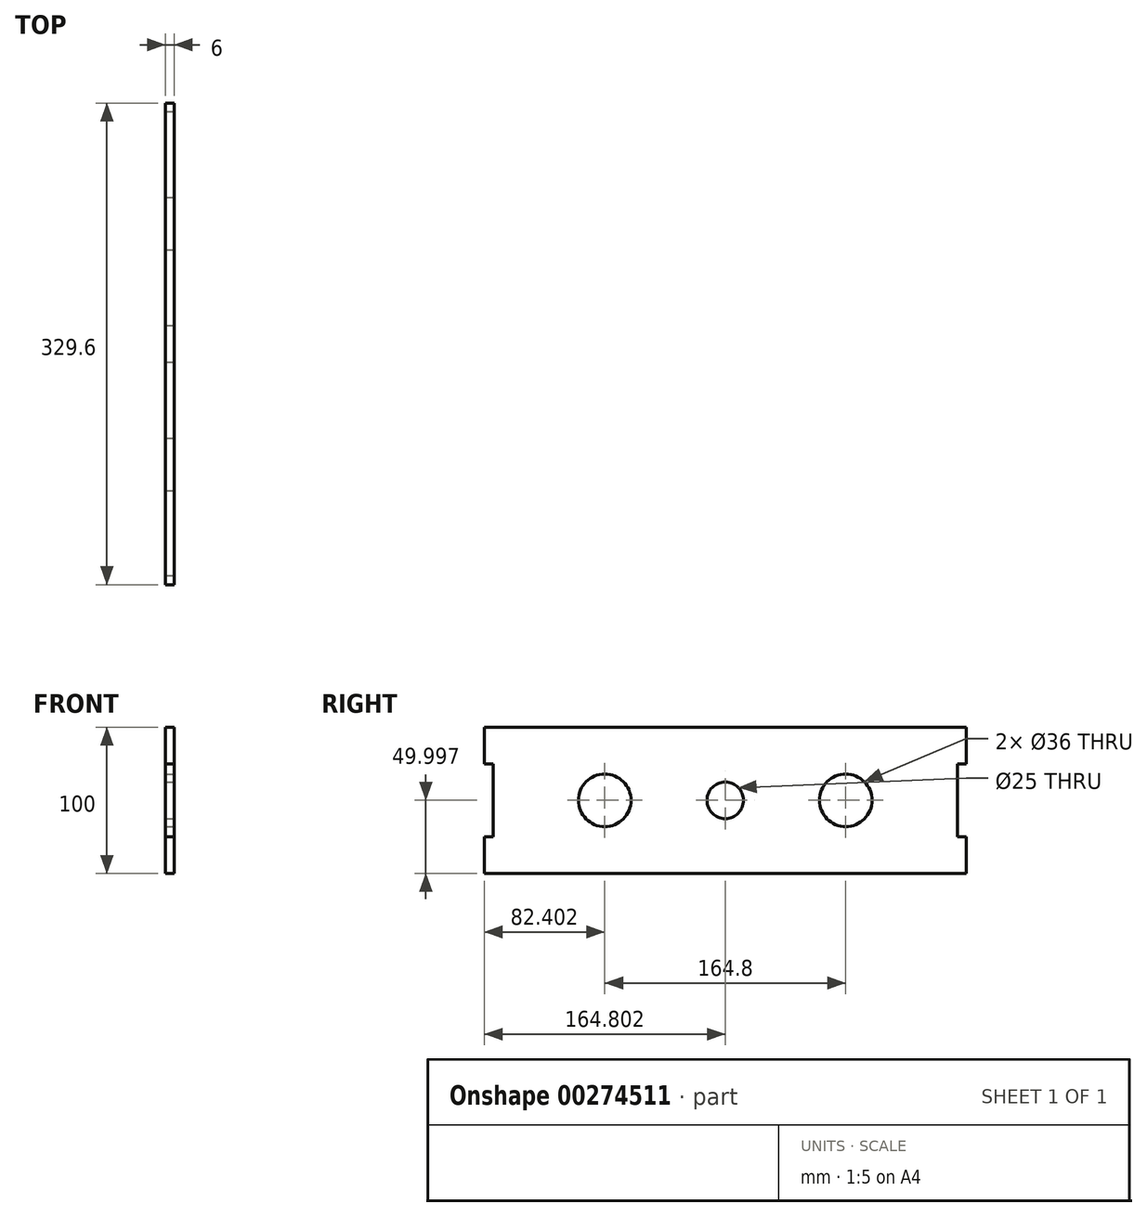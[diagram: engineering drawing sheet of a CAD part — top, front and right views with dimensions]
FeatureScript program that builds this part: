
annotation { "Feature Type Name" : "Feature", "Feature Type Description" : "" }
export const myFeature = defineFeature(function(context is Context, id is Id, definition is map)
    precondition{}
    {
        {
            var Q0;
            Q0=qCreatedBy(makeId("Right.planeOp"),FACE);
            var sketch = newSketch(context, id + "F0", { "sketchPlane" : qUnion([Q0])});
            skLineSegment(sketch, "E0.bottom", {"start": v(-256.02, 58.03) * mm, "end": v(61.58, 58.03) * mm});
            skLineSegment(sketch, "E0.top", {"start": v(-256.02, -41.97) * mm, "end": v(61.58, -41.97) * mm});
            skLineSegment(sketch, "E1", {"start": v(-256.02, 58.03) * mm, "end": v(-262.02, 58.03) * mm});
            skLineSegment(sketch, "E2", {"start": v(-262.02, 58.03) * mm, "end": v(-262.02, 33.03) * mm});
            skLineSegment(sketch, "E3", {"start": v(-262.02, 33.03) * mm, "end": v(-256.02, 33.03) * mm});
            skLineSegment(sketch, "E4", {"start": v(-256.02, 33.03) * mm, "end": v(-256.02, -16.97) * mm});
            skLineSegment(sketch, "E5", {"start": v(-256.02, -16.97) * mm, "end": v(-262.02, -16.97) * mm});
            skLineSegment(sketch, "E6", {"start": v(-262.02, -16.97) * mm, "end": v(-262.02, -41.97) * mm});
            skLineSegment(sketch, "E7", {"start": v(-262.02, -41.97) * mm, "end": v(-256.02, -41.97) * mm});
            skLineSegment(sketch, "E8", {"start": v(61.58, 58.03) * mm, "end": v(67.58, 58.03) * mm});
            skLineSegment(sketch, "E9", {"start": v(67.58, 58.03) * mm, "end": v(67.58, 33.03) * mm});
            skLineSegment(sketch, "E10", {"start": v(67.58, -16.97) * mm, "end": v(67.58, -41.97) * mm});
            skLineSegment(sketch, "E11", {"start": v(67.58, -41.97) * mm, "end": v(61.58, -41.97) * mm});
            skLineSegment(sketch, "E12", {"start": v(67.58, -16.97) * mm, "end": v(61.58, -16.97) * mm});
            skLineSegment(sketch, "E13", {"start": v(61.58, -16.97) * mm, "end": v(61.58, 33.03) * mm});
            skLineSegment(sketch, "E14", {"start": v(61.58, 33.03) * mm, "end": v(67.58, 33.03) * mm});
            skSolve(sketch);
        }
        {
            var Q0;
            Q0=makeQuery(id+"F0.imprint","IMPRINT",FACE,{"disambiguationData":[TD([[makeQuery(id+"F0.imprint","IMPRINT",EDGE,{"derivedFrom":sQuery(id+"F0.wireOp",EDGE,"E0.bottom")}),-1.0]])]});
            extrude(context, id + "F1", {"entities" : qUnion([Q0]), "depth" : 6 * mm});
        }
        {
            var Q0;
            Q0=makeQuery(id+"F1.opExtrude","CAP_FACE",FACE,{"disambiguationData":[OSD([sQuery(id+"F0.wireOp",EDGE,"E0.bottom"),sQuery(id+"F0.wireOp",EDGE,"E0.top"),sQuery(id+"F0.wireOp",EDGE,"E1"),sQuery(id+"F0.wireOp",EDGE,"E2"),sQuery(id+"F0.wireOp",EDGE,"E3"),sQuery(id+"F0.wireOp",EDGE,"E4"),sQuery(id+"F0.wireOp",EDGE,"E5"),sQuery(id+"F0.wireOp",EDGE,"E6"),sQuery(id+"F0.wireOp",EDGE,"E7"),sQuery(id+"F0.wireOp",EDGE,"E8"),sQuery(id+"F0.wireOp",EDGE,"E9"),sQuery(id+"F0.wireOp",EDGE,"E10"),sQuery(id+"F0.wireOp",EDGE,"E11"),sQuery(id+"F0.wireOp",EDGE,"E12"),sQuery(id+"F0.wireOp",EDGE,"E13"),sQuery(id+"F0.wireOp",EDGE,"E14")])],"isStart":false});
            var sketch = newSketch(context, id + "F2", { "sketchPlane" : qUnion([Q0])});
            skCircle(sketch, "E15", {"center": v(-179.62, 8.03) * mm, "radius": 18 * mm});
            skCircle(sketch, "E16", {"center": v(-97.22, 8.03) * mm, "radius": 12.5 * mm});
            skCircle(sketch, "E17", {"center": v(-14.82, 8.03) * mm, "radius": 18 * mm});
            skSolve(sketch);
        }
        {
            var Q0;
            Q0 = qSketchRegion(id + "F2", true);
            extrude(context, id + "F3", {"entities" : qUnion([Q0]), "operationType" : NewBodyOperationType.REMOVE, "oppositeDirection" : true, "depth" : 25 * mm});
        }
    });
